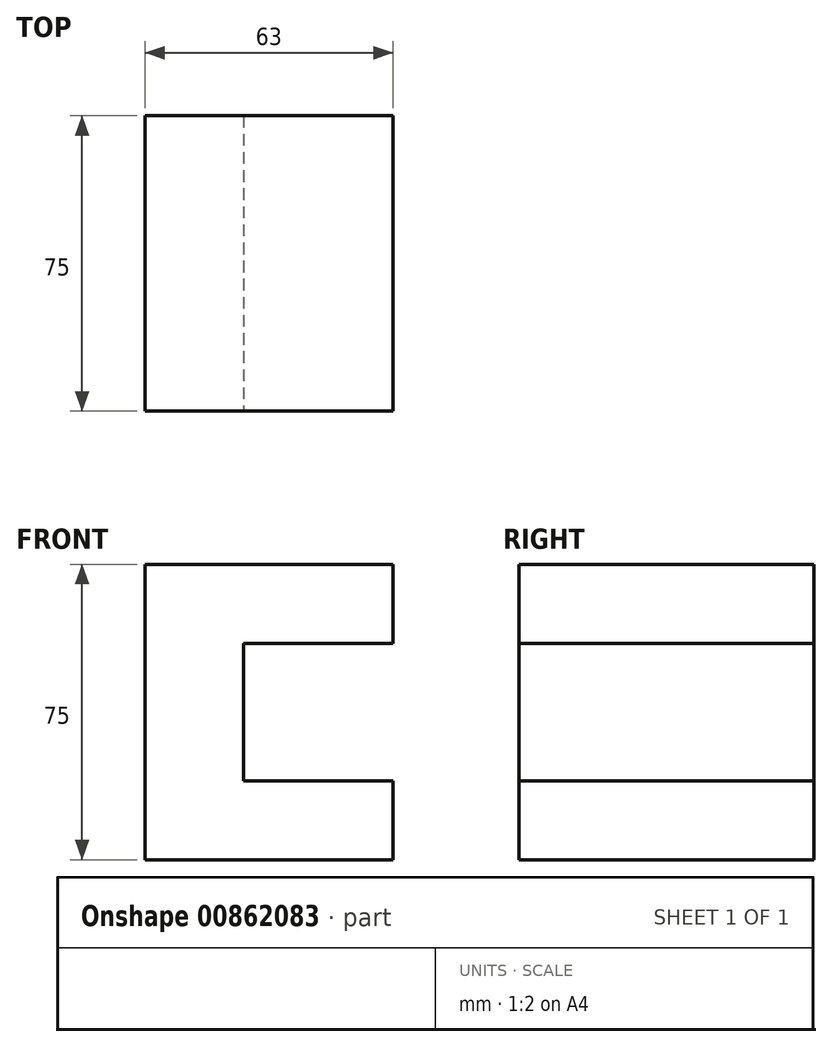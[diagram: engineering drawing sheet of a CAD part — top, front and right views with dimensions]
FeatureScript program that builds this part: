
annotation { "Feature Type Name" : "Feature", "Feature Type Description" : "" }
export const myFeature = defineFeature(function(context is Context, id is Id, definition is map)
    precondition{}
    {
        {
            var Q0;
            Q0=qCreatedBy(makeId("Top.planeOp"),FACE);
            var sketch = newSketch(context, id + "F0", { "sketchPlane" : qUnion([Q0])});
            skLineSegment(sketch, "E0.bottom", {"start": v(0, 0) * mm, "end": v(63, 0) * mm});
            skLineSegment(sketch, "E0.top", {"start": v(0, 75) * mm, "end": v(63, 75) * mm});
            skLineSegment(sketch, "E0.left", {"start": v(0, 0) * mm, "end": v(0, 75) * mm});
            skLineSegment(sketch, "E0.right", {"start": v(63, 0) * mm, "end": v(63, 75) * mm});
            skSolve(sketch);
        }
        {
            var Q0;
            Q0=makeQuery(id+"F0.imprint","IMPRINT",FACE,{"disambiguationData":[TD([[makeQuery(id+"F0.imprint","IMPRINT",EDGE,{"derivedFrom":sQuery(id+"F0.wireOp",EDGE,"E0.bottom")}),1.0]])]});
            extrude(context, id + "F1", {"entities" : qUnion([Q0]), "depth" : 75 * mm, "offsetDistance" : 25 * mm});
        }
        {
            var Q0;
            Q0=makeQuery(id+"F1.opExtrude","SWEPT_FACE",FACE,{"disambiguationData":[OSD([sQuery(id+"F0.wireOp",EDGE,"E0.right")])]});
            var sketch = newSketch(context, id + "F2", { "sketchPlane" : qUnion([Q0])});
            skLineSegment(sketch, "E1", {"start": v(37.5, 20) * mm, "end": v(0, 20) * mm});
            skLineSegment(sketch, "E2.bottom", {"start": v(0, 20) * mm, "end": v(75, 20) * mm});
            skLineSegment(sketch, "E2.top", {"start": v(0, 55) * mm, "end": v(75, 55) * mm});
            skLineSegment(sketch, "E2.left", {"start": v(0, 20) * mm, "end": v(0, 55) * mm});
            skLineSegment(sketch, "E2.right", {"start": v(75, 20) * mm, "end": v(75, 55) * mm});
            skSolve(sketch);
        }
        {
            var Q0;
            Q0=makeQuery(id+"F2.imprint","IMPRINT",FACE,{"disambiguationData":[TD([[makeQuery(id+"F2.imprint","IMPRINT",EDGE,{"derivedFrom":sQuery(id+"F2.wireOp",EDGE,"E2.top")}),-1.0]])]});
            extrude(context, id + "F3", {"entities" : qUnion([Q0]), "operationType" : NewBodyOperationType.REMOVE, "oppositeDirection" : true, "depth" : 38 * mm, "offsetDistance" : 25 * mm});
        }
    });
